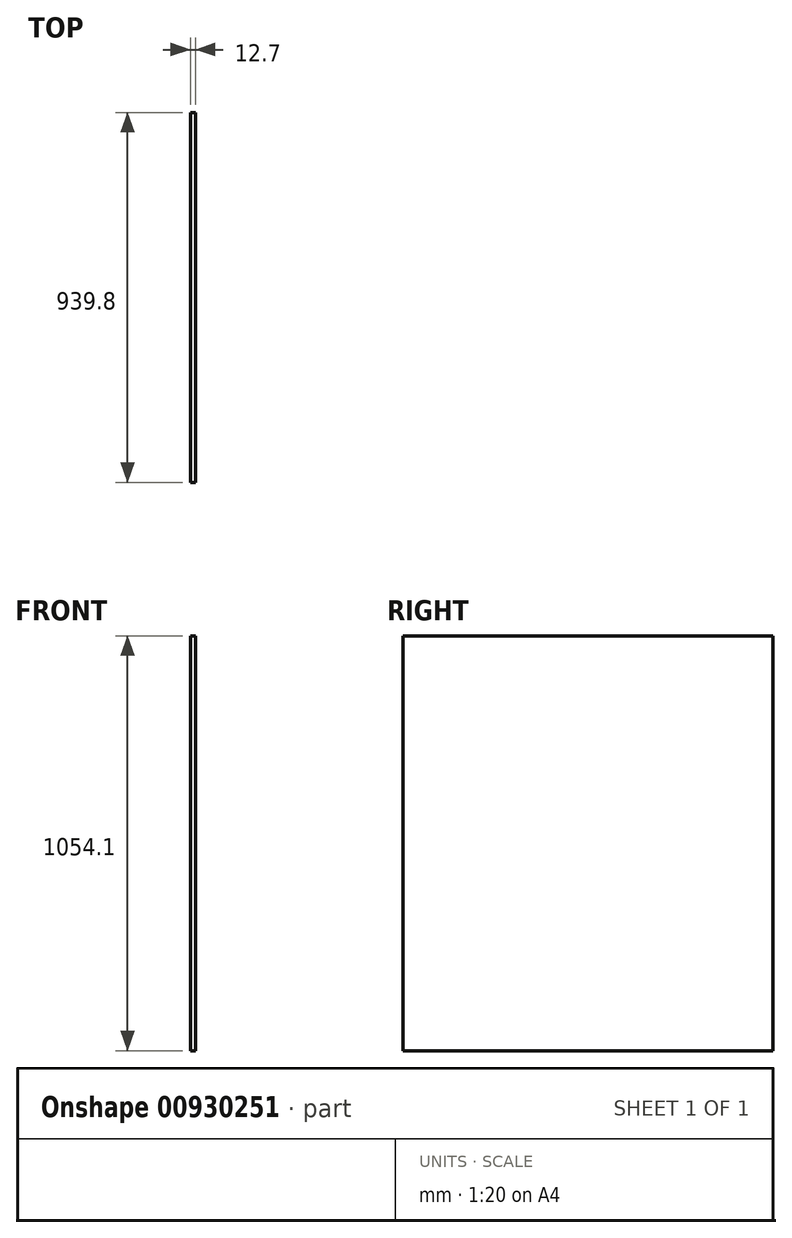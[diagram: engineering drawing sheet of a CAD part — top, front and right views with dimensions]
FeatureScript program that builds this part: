
annotation { "Feature Type Name" : "Feature", "Feature Type Description" : "" }
export const myFeature = defineFeature(function(context is Context, id is Id, definition is map)
    precondition{}
    {
        {
            var Q0;
            Q0=qCreatedBy(makeId("Right.planeOp"),FACE);
            var sketch = newSketch(context, id + "F0", { "sketchPlane" : qUnion([Q0])});
            skLineSegment(sketch, "E0.bottom", {"start": v(469.9, -527.05) * mm, "end": v(-469.9, -527.05) * mm});
            skLineSegment(sketch, "E0.top", {"start": v(469.9, 527.05) * mm, "end": v(-469.9, 527.05) * mm});
            skLineSegment(sketch, "E0.left", {"start": v(469.9, -527.05) * mm, "end": v(469.9, 527.05) * mm});
            skLineSegment(sketch, "E0.right", {"start": v(-469.9, -527.05) * mm, "end": v(-469.9, 527.05) * mm});
            skPoint(sketch, "E0.middle", {"position": v(0, 0) * mm});
            skSolve(sketch);
        }
        {
            var Q0;
            Q0=qSketchRegion(id+"F0",true);
            extrude(context, id + "F1", {"entities" : qUnion([Q0]), "endBound" : BoundingType.SYMMETRIC, "depth" : 12.7 * mm});
        }
    });
